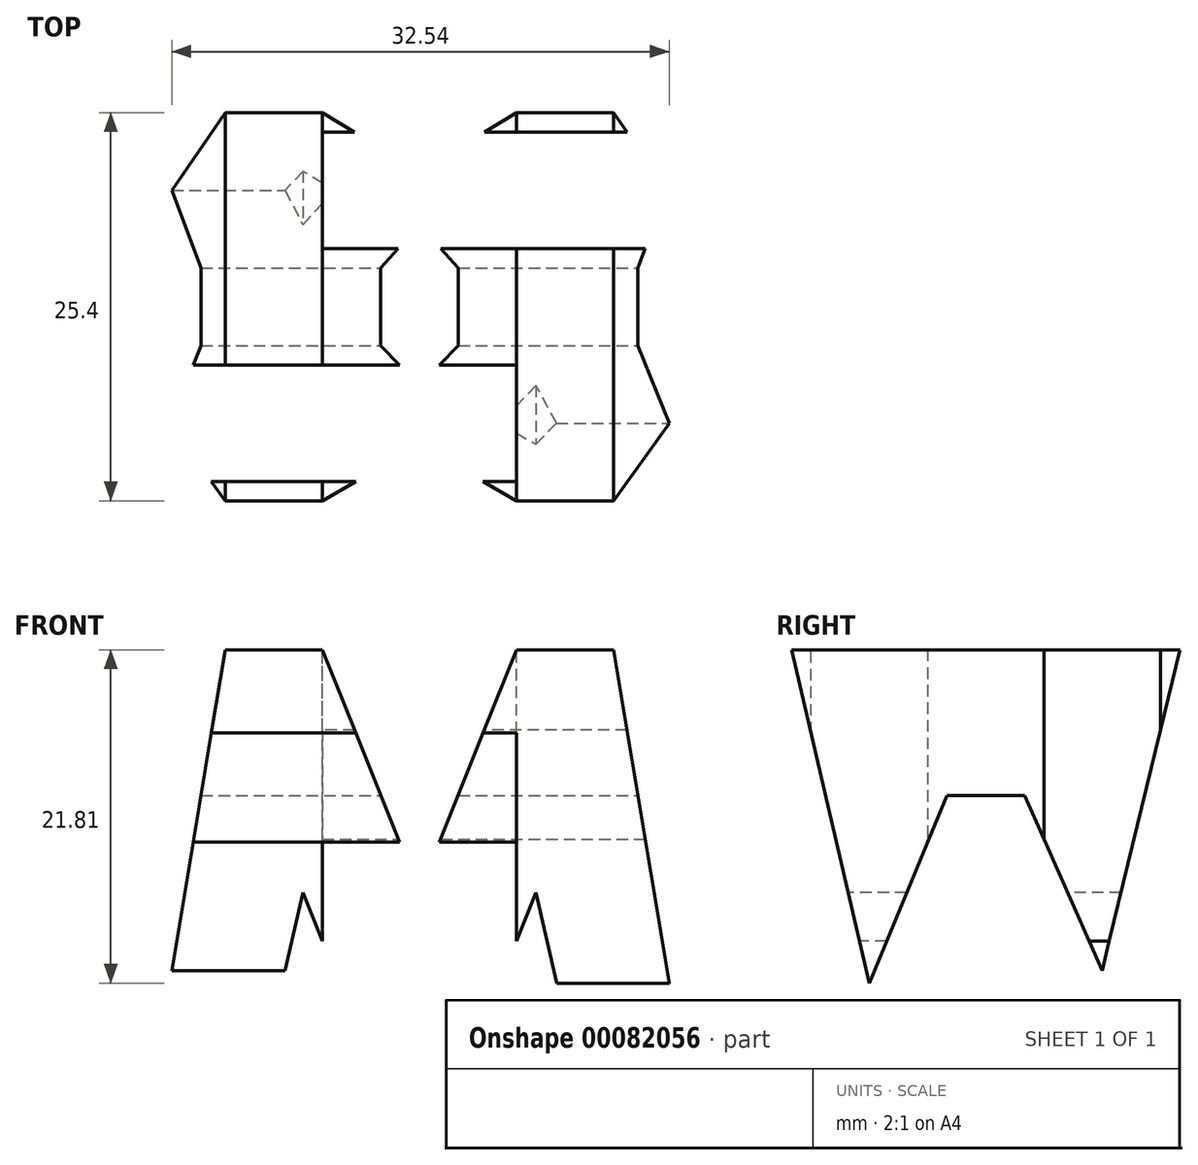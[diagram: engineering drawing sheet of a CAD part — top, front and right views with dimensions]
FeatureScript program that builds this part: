
annotation { "Feature Type Name" : "Feature", "Feature Type Description" : "" }
export const myFeature = defineFeature(function(context is Context, id is Id, definition is map)
    precondition{}
    {
        {
            var Q0;
            Q0=qCreatedBy(makeId("Front.planeOp"),FACE);
            var sketch = newSketch(context, id + "F0", { "sketchPlane" : qUnion([Q0])});
            skLineSegment(sketch, "E0", {"start": v(0, 0) * mm, "end": v(0, 38.1) * mm});
            skLineSegment(sketch, "E1", {"start": v(0, 38.1) * mm, "end": v(38.1, 38.1) * mm});
            skLineSegment(sketch, "E2", {"start": v(38.1, 38.1) * mm, "end": v(38.1, 0) * mm});
            skLineSegment(sketch, "E3", {"start": v(38.1, 0) * mm, "end": v(0, 0) * mm});
            skSolve(sketch);
        }
        {
            var Q0;
            Q0=makeQuery(id+"F0.imprint","IMPRINT",FACE,{"disambiguationData":[TD([[makeQuery(id+"F0.imprint","IMPRINT",EDGE,{"derivedFrom":sQuery(id+"F0.wireOp",EDGE,"E0")}),-1.0]])]});
            extrude(context, id + "F1", {"entities" : qUnion([Q0]), "depth" : 38.1 * mm});
        }
        {
            var Q0;
            Q0=qCreatedBy(makeId("Front.planeOp"),FACE);
            cPlane(context, id + "F2", {"entities" : qUnion([Q0]), "cplaneType" : CPlaneType.OFFSET, "offset" : 38.1 * mm, "width" : 152.4 * mm, "height" : 152.4 * mm});
        }
        {
            var Q0;
            Q0=qCreatedBy(makeId("Right.planeOp"),FACE);
            cPlane(context, id + "F3", {"entities" : qUnion([Q0]), "cplaneType" : CPlaneType.OFFSET, "offset" : 38.1 * mm, "width" : 152.4 * mm, "height" : 152.4 * mm});
        }
        {
            var Q0;
            Q0=qCreatedBy(makeId("Top.planeOp"),FACE);
            cPlane(context, id + "F4", {"entities" : qUnion([Q0]), "cplaneType" : CPlaneType.OFFSET, "offset" : 38.1 * mm, "width" : 152.4 * mm, "height" : 152.4 * mm});
        }
        {
            var Q0;
            Q0=qCreatedBy(id+"F3.planeOp",FACE);
            var sketch = newSketch(context, id + "F5", { "sketchPlane" : qUnion([Q0])});
            skLineSegment(sketch, "E4", {"start": v(0, 0) * mm, "end": v(0, 38.1) * mm});
            skLineSegment(sketch, "E5", {"start": v(0, 38.1) * mm, "end": v(-38.1, 38.1) * mm});
            skLineSegment(sketch, "E6", {"start": v(-38.1, 38.1) * mm, "end": v(-38.1, 0) * mm});
            skLineSegment(sketch, "E7", {"start": v(-38.1, 0) * mm, "end": v(0, 0) * mm});
            skLineSegment(sketch, "E8", {"start": v(-38.1, 38.1) * mm, "end": v(-31.75, 0) * mm});
            skLineSegment(sketch, "E9", {"start": v(-31.75, 0) * mm, "end": v(-25.4, 0) * mm});
            skLineSegment(sketch, "E10", {"start": v(-25.4, 0) * mm, "end": v(-18.06, 15.88) * mm});
            skLineSegment(sketch, "E11", {"start": v(-18.06, 15.88) * mm, "end": v(-12.7, 0) * mm});
            skLineSegment(sketch, "E12", {"start": v(-12.7, 0) * mm, "end": v(-6.35, 0) * mm});
            skLineSegment(sketch, "E13", {"start": v(-6.35, 0) * mm, "end": v(0, 38.1) * mm});
            skLineSegment(sketch, "E14", {"start": v(0, 38.1) * mm, "end": v(-6.35, 38.1) * mm});
            skLineSegment(sketch, "E15", {"start": v(-6.35, 38.1) * mm, "end": v(-11.43, 17.11) * mm});
            skLineSegment(sketch, "E16", {"start": v(-11.43, 17.11) * mm, "end": v(-16.51, 28.57) * mm});
            skLineSegment(sketch, "E17", {"start": v(-16.51, 28.57) * mm, "end": v(-21.6, 28.57) * mm});
            skLineSegment(sketch, "E18", {"start": v(-21.6, 28.57) * mm, "end": v(-26.67, 16.29) * mm});
            skLineSegment(sketch, "E19", {"start": v(-26.67, 16.29) * mm, "end": v(-31.75, 38.1) * mm});
            skLineSegment(sketch, "E20", {"start": v(-31.75, 38.1) * mm, "end": v(-38.1, 38.1) * mm});
            skSolve(sketch);
        }
        {
            var Q0;
            Q0=makeQuery(id+"F5.imprint","IMPRINT",FACE,{"disambiguationData":[TD([[makeQuery(id+"F5.imprint","IMPRINT",EDGE,{"derivedFrom":sQuery(id+"F5.wireOp",EDGE,"E5")}),1.0]])]});
            var Q1;
            {var subQ0=sQuery(id+"F5.wireOp",EDGE,"E6");Q1=makeQuery(id+"F5.imprint","IMPRINT",FACE,{"disambiguationData":[TD([[makeQuery(id+"F5.imprint","IMPRINT",EDGE,{"derivedFrom":subQ0}),1.0]])]});}
            var Q2;
            {var subQ0=sQuery(id+"F5.wireOp",EDGE,"E10");Q2=makeQuery(id+"F5.imprint","IMPRINT",FACE,{"disambiguationData":[TD([[makeQuery(id+"F5.imprint","IMPRINT",EDGE,{"derivedFrom":subQ0}),-1.0]])]});}
            var Q3;
            {var subQ0=sQuery(id+"F5.wireOp",EDGE,"E4");Q3=makeQuery(id+"F5.imprint","IMPRINT",FACE,{"disambiguationData":[TD([[makeQuery(id+"F5.imprint","IMPRINT",EDGE,{"derivedFrom":subQ0}),1.0]])]});}
            extrude(context, id + "F6", {"entities" : qUnion([Q0, Q1, Q2, Q3]), "operationType" : NewBodyOperationType.REMOVE, "oppositeDirection" : true, "depth" : 38.1 * mm});
        }
        {
            var Q0;
            Q0=qCreatedBy(id+"F2.planeOp",FACE);
            var sketch = newSketch(context, id + "F7", { "sketchPlane" : qUnion([Q0])});
            skLineSegment(sketch, "E21", {"start": v(0, 0) * mm, "end": v(0, 38.1) * mm});
            skLineSegment(sketch, "E22", {"start": v(0, 38.1) * mm, "end": v(38.1, 38.1) * mm});
            skLineSegment(sketch, "E23", {"start": v(38.1, 38.1) * mm, "end": v(38.1, 0) * mm});
            skLineSegment(sketch, "E24", {"start": v(38.1, 0) * mm, "end": v(0, 0) * mm});
            skLineSegment(sketch, "E25", {"start": v(0, 0) * mm, "end": v(6.35, 38.1) * mm});
            skLineSegment(sketch, "E26", {"start": v(6.35, 38.1) * mm, "end": v(12.7, 38.1) * mm});
            skLineSegment(sketch, "E27", {"start": v(12.7, 38.1) * mm, "end": v(19.05, 22.22) * mm});
            skLineSegment(sketch, "E28", {"start": v(19.05, 22.23) * mm, "end": v(25.4, 38.1) * mm});
            skLineSegment(sketch, "E29", {"start": v(25.4, 38.1) * mm, "end": v(31.75, 38.1) * mm});
            skLineSegment(sketch, "E30", {"start": v(31.75, 38.1) * mm, "end": v(38.1, 0) * mm});
            skLineSegment(sketch, "E31", {"start": v(31.75, 0) * mm, "end": v(26.67, 22.23) * mm});
            skLineSegment(sketch, "E32", {"start": v(26.67, 22.23) * mm, "end": v(21.59, 9.53) * mm});
            skLineSegment(sketch, "E33", {"start": v(21.59, 9.53) * mm, "end": v(16.51, 9.53) * mm});
            skLineSegment(sketch, "E34", {"start": v(16.51, 9.52) * mm, "end": v(11.43, 22.22) * mm});
            skLineSegment(sketch, "E35", {"start": v(11.43, 22.23) * mm, "end": v(6.35, 0) * mm});
            skLineSegment(sketch, "E36", {"start": v(6.35, 0) * mm, "end": v(0, 0) * mm});
            skSolve(sketch);
        }
        {
            var Q0;
            {var subQ0=sQuery(id+"F7.wireOp",EDGE,"E31");Q0=makeQuery(id+"F7.imprint","IMPRINT",FACE,{"disambiguationData":[TD([[makeQuery(id+"F7.imprint","IMPRINT",EDGE,{"derivedFrom":subQ0}),1.0]])]});}
            var Q1;
            {var subQ0=sQuery(id+"F7.wireOp",EDGE,"E21");Q1=makeQuery(id+"F7.imprint","IMPRINT",FACE,{"disambiguationData":[TD([[makeQuery(id+"F7.imprint","IMPRINT",EDGE,{"derivedFrom":subQ0}),-1.0]])]});}
            var Q2;
            {var subQ0=sQuery(id+"F7.wireOp",EDGE,"E27");Q2=makeQuery(id+"F7.imprint","IMPRINT",FACE,{"disambiguationData":[TD([[makeQuery(id+"F7.imprint","IMPRINT",EDGE,{"derivedFrom":subQ0}),1.0]])]});}
            var Q3;
            {var subQ0=sQuery(id+"F7.wireOp",EDGE,"E23");Q3=makeQuery(id+"F7.imprint","IMPRINT",FACE,{"disambiguationData":[TD([[makeQuery(id+"F7.imprint","IMPRINT",EDGE,{"derivedFrom":subQ0}),-1.0]])]});}
            extrude(context, id + "F8", {"entities" : qUnion([Q0, Q1, Q2, Q3]), "operationType" : NewBodyOperationType.REMOVE, "oppositeDirection" : true, "depth" : 38.1 * mm});
        }
        {
            var Q0;
            Q0=qCreatedBy(id+"F4.planeOp",FACE);
            var sketch = newSketch(context, id + "F9", { "sketchPlane" : qUnion([Q0])});
            skLineSegment(sketch, "E37", {"start": v(0, 0) * mm, "end": v(0, -38.1) * mm});
            skLineSegment(sketch, "E38", {"start": v(0, -38.1) * mm, "end": v(38.1, -38.1) * mm});
            skLineSegment(sketch, "E39", {"start": v(38.1, -38.1) * mm, "end": v(38.1, 0) * mm});
            skLineSegment(sketch, "E40", {"start": v(38.1, 0) * mm, "end": v(0, 0) * mm});
            skLineSegment(sketch, "E41", {"start": v(38.1, -7.62) * mm, "end": v(12.7, -7.62) * mm});
            skLineSegment(sketch, "E42", {"start": v(12.7, -7.62) * mm, "end": v(12.7, -15.24) * mm});
            skLineSegment(sketch, "E43", {"start": v(12.7, -15.24) * mm, "end": v(38.1, -15.24) * mm});
            skLineSegment(sketch, "E44", {"start": v(0, -22.86) * mm, "end": v(25.4, -22.86) * mm});
            skLineSegment(sketch, "E45", {"start": v(25.4, -22.86) * mm, "end": v(25.4, -30.48) * mm});
            skLineSegment(sketch, "E46", {"start": v(25.4, -30.48) * mm, "end": v(0, -30.48) * mm});
            skSolve(sketch);
        }
        {
            var Q0;
            {var subQ0=sQuery(id+"F9.wireOp",EDGE,"E41");Q0=makeQuery(id+"F9.imprint","IMPRINT",FACE,{"disambiguationData":[TD([[makeQuery(id+"F9.imprint","IMPRINT",EDGE,{"derivedFrom":subQ0}),1.0]])]});}
            var Q1;
            {var subQ0=sQuery(id+"F9.wireOp",EDGE,"E44");Q1=makeQuery(id+"F9.imprint","IMPRINT",FACE,{"disambiguationData":[TD([[makeQuery(id+"F9.imprint","IMPRINT",EDGE,{"derivedFrom":subQ0}),-1.0]])]});}
            extrude(context, id + "F10", {"entities" : qUnion([Q0, Q1]), "operationType" : NewBodyOperationType.REMOVE, "oppositeDirection" : true, "depth" : 38.1 * mm});
        }
    });
